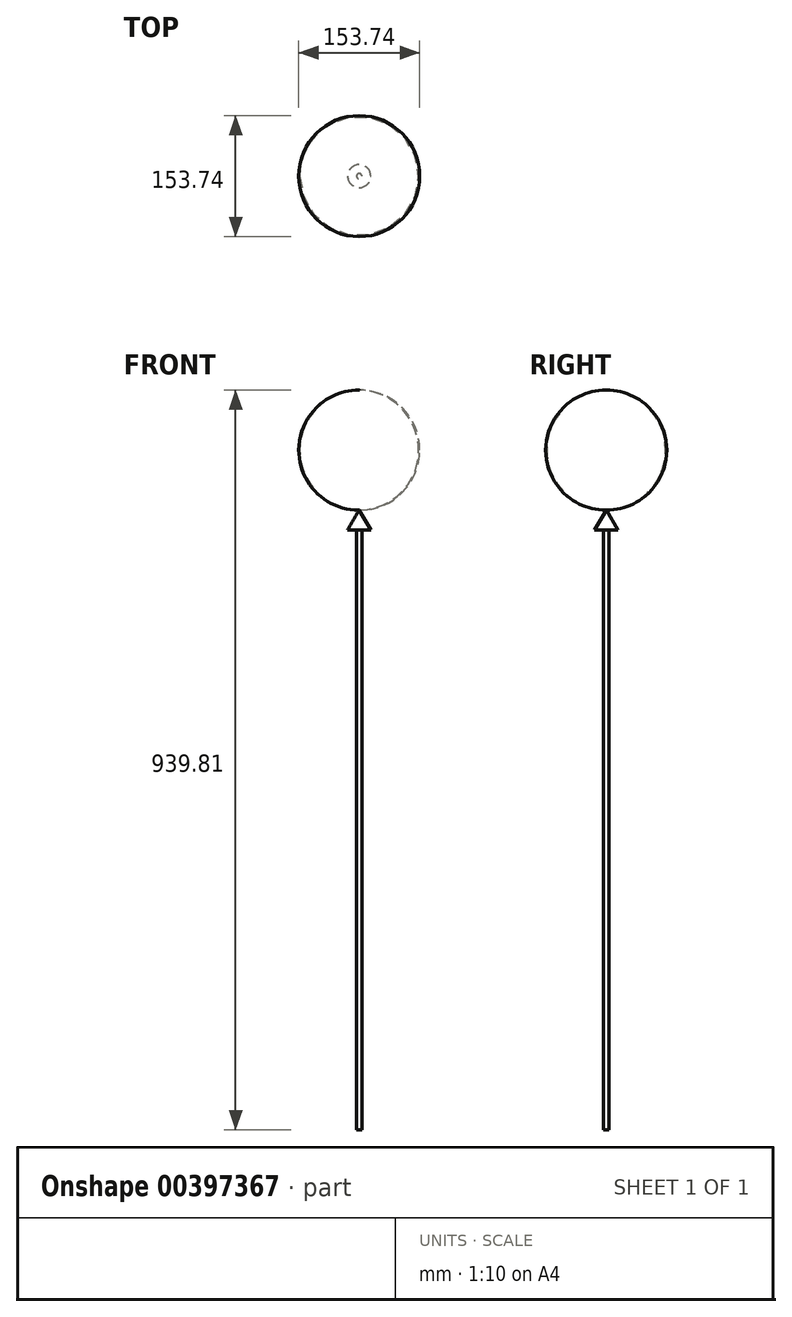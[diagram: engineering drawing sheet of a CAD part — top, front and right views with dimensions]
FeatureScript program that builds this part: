
annotation { "Feature Type Name" : "Feature", "Feature Type Description" : "" }
export const myFeature = defineFeature(function(context is Context, id is Id, definition is map)
    precondition{}
    {
        {
            var Q0;
            Q0=qCreatedBy(makeId("Front.planeOp"),FACE);
            var sketch = newSketch(context, id + "F0", { "sketchPlane" : qUnion([Q0])});
            skLineSegment(sketch, "E0", {"start": v(0, 76.1) * mm, "end": v(0, -76.3) * mm});
            skArc(sketch, "E1", {"start": v(0, 76.1) * mm, "mid": v(-76.87, -0.1) * mm, "end": v(0, -76.3) * mm});
            skCircle(sketch, "E2.cCircle", {"center": v(0, -93.24) * mm, "radius": 8.47 * mm, "construction": true});
            skLineSegment(sketch, "E2.2", {"start": v(-14.66, -101.7) * mm, "end": v(0, -76.3) * mm});
            skPoint(sketch, "E2.0.midPoint", {"position": v(7.33, -89) * mm});
            skLineSegment(sketch, "E3", {"start": v(0, -76.3) * mm, "end": v(0, -101.7) * mm});
            skLineSegment(sketch, "E4", {"start": v(-14.66, -101.7) * mm, "end": v(0, -101.7) * mm});
            skSolve(sketch);
        }
        {
            var Q0;
            Q0=makeQuery(id+"F0.imprint","IMPRINT",FACE,{"disambiguationData":[TD([[makeQuery(id+"F0.imprint","IMPRINT",EDGE,{"derivedFrom":sQuery(id+"F0.wireOp",EDGE,"E0")}),-1.0]])]});
            var Q1;
            Q1=makeQuery(id+"F0.imprint","IMPRINT",FACE,{"disambiguationData":[TD([[makeQuery(id+"F0.imprint","IMPRINT",EDGE,{"derivedFrom":sQuery(id+"F0.wireOp",EDGE,"E2.2")}),-1.0]])]});
            var Q2;
            Q2=sQuery(id+"F0.wireOp",EDGE,"E0");
            revolve(context, id + "F1", {"entities" : qUnion([Q0, Q1]), "axis" : qUnion([Q2]), "revolveType" : RevolveType.FULL});
        }
        {
            var Q0;
            Q0=makeQuery(id+"F1.opRevolve","SWEPT_FACE",FACE,{"disambiguationData":[OSD([sQuery(id+"F0.wireOp",EDGE,"E4")])]});
            var sketch = newSketch(context, id + "F2", { "sketchPlane" : qUnion([Q0])});
            skCircle(sketch, "E5", {"center": v(0, 0) * mm, "radius": 3.35 * mm});
            skSolve(sketch);
        }
        {
            var Q0;
            Q0=makeQuery(id+"F2.imprint","IMPRINT",FACE,{"disambiguationData":[TD([[makeQuery(id+"F2.imprint","IMPRINT",EDGE,{"derivedFrom":sQuery(id+"F2.wireOp",EDGE,"E5")}),1.0]])]});
            extrude(context, id + "F3", {"entities" : qUnion([Q0]), "operationType" : NewBodyOperationType.ADD, "depth" : 762 * mm});
        }
        {
            var Q0;
            Q0=qCreatedBy(makeId("Front.planeOp"),FACE);
            cPlane(context, id + "F4", {"entities" : qUnion([Q0]), "cplaneType" : CPlaneType.OFFSET, "offset" : 77.47 * mm, "oppositeDirection" : true, "width" : 152.4 * mm, "height" : 152.4 * mm});
        }
    });
